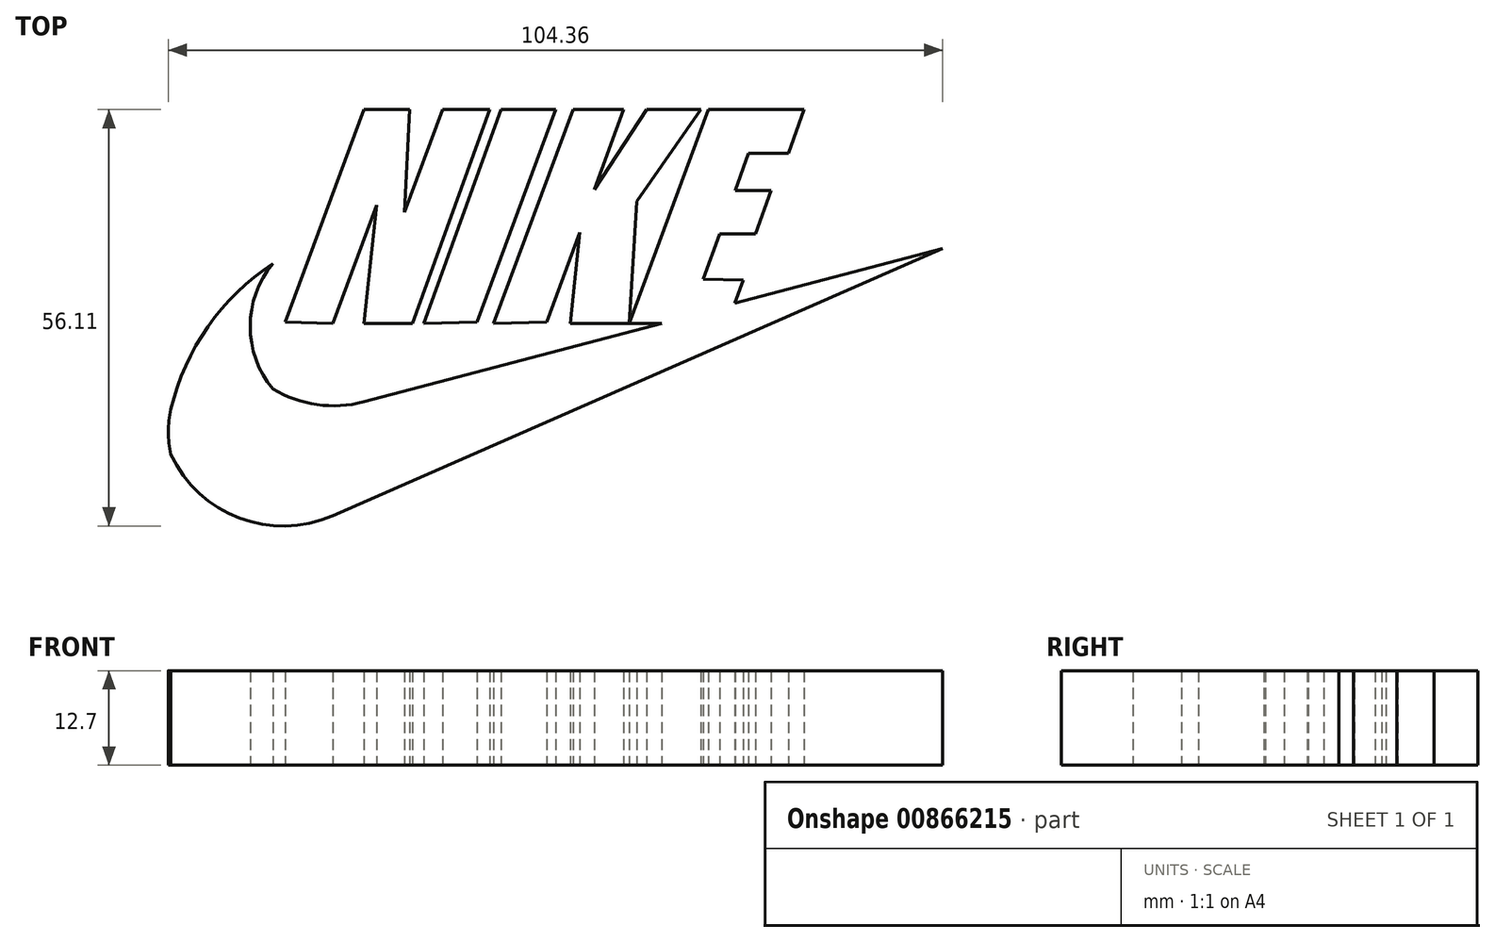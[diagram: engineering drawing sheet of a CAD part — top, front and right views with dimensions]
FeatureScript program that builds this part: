
annotation { "Feature Type Name" : "Feature", "Feature Type Description" : "" }
export const myFeature = defineFeature(function(context is Context, id is Id, definition is map)
    precondition{}
    {
        {
            var Q0;
            Q0=qCreatedBy(makeId("Top.planeOp"),FACE);
            var sketch = newSketch(context, id + "F0", { "sketchPlane" : qUnion([Q0])});
            skLineSegment(sketch, "E0", {"start": v(-47.42, 31.24) * mm, "end": v(-36.81, 59.87) * mm});
            skLineSegment(sketch, "E1", {"start": v(-36.81, 59.87) * mm, "end": v(-30.63, 59.87) * mm});
            skLineSegment(sketch, "E2", {"start": v(-30.63, 59.87) * mm, "end": v(-31.32, 46.03) * mm});
            skLineSegment(sketch, "E3", {"start": v(-31.32, 46.03) * mm, "end": v(-26.16, 59.87) * mm});
            skLineSegment(sketch, "E4", {"start": v(-26.16, 59.87) * mm, "end": v(-19.85, 59.87) * mm});
            skLineSegment(sketch, "E5", {"start": v(-19.85, 59.87) * mm, "end": v(-30.25, 31.03) * mm});
            skLineSegment(sketch, "E6", {"start": v(-30.25, 31.03) * mm, "end": v(-36.81, 31.03) * mm});
            skLineSegment(sketch, "E7", {"start": v(-36.81, 31.03) * mm, "end": v(-35.1, 46.96) * mm});
            skLineSegment(sketch, "E8", {"start": v(-35.1, 46.96) * mm, "end": v(-40.99, 31.03) * mm});
            skLineSegment(sketch, "E9", {"start": v(-40.99, 31.03) * mm, "end": v(-47.42, 31.24) * mm});
            skLineSegment(sketch, "E10", {"start": v(-28.7, 31.03) * mm, "end": v(-18.3, 59.87) * mm});
            skLineSegment(sketch, "E11", {"start": v(-18.3, 59.87) * mm, "end": v(-10.92, 59.87) * mm});
            skLineSegment(sketch, "E12", {"start": v(-10.92, 59.87) * mm, "end": v(-21.53, 31.24) * mm});
            skLineSegment(sketch, "E13", {"start": v(-21.53, 31.24) * mm, "end": v(-28.7, 31.03) * mm});
            skLineSegment(sketch, "E14", {"start": v(-19.3, 31.03) * mm, "end": v(-8.61, 59.87) * mm});
            skLineSegment(sketch, "E15", {"start": v(-8.61, 59.87) * mm, "end": v(-1.83, 59.87) * mm});
            skLineSegment(sketch, "E16", {"start": v(-1.83, 59.87) * mm, "end": v(-5.71, 49.1) * mm});
            skLineSegment(sketch, "E17", {"start": v(-5.71, 49.1) * mm, "end": v(1.3, 59.87) * mm});
            skLineSegment(sketch, "E18", {"start": v(1.3, 59.87) * mm, "end": v(8.6, 59.87) * mm});
            skLineSegment(sketch, "E19", {"start": v(8.6, 59.87) * mm, "end": v(0, 47.53) * mm});
            skLineSegment(sketch, "E20", {"start": v(0, 47.53) * mm, "end": v(-1.04, 31.03) * mm});
            skLineSegment(sketch, "E21", {"start": v(-1.04, 31.03) * mm, "end": v(-9, 31.03) * mm});
            skLineSegment(sketch, "E22", {"start": v(-9, 31.03) * mm, "end": v(-7.69, 43.28) * mm});
            skLineSegment(sketch, "E23", {"start": v(-7.69, 43.28) * mm, "end": v(-12.14, 31.24) * mm});
            skLineSegment(sketch, "E24", {"start": v(-12.14, 31.24) * mm, "end": v(-19.3, 31.03) * mm});
            skLineSegment(sketch, "E25", {"start": v(-1.04, 31.03) * mm, "end": v(9.64, 59.87) * mm});
            skLineSegment(sketch, "E26", {"start": v(9.64, 59.87) * mm, "end": v(22.52, 59.87) * mm});
            skLineSegment(sketch, "E27", {"start": v(22.52, 59.87) * mm, "end": v(20.4, 54) * mm});
            skLineSegment(sketch, "E28", {"start": v(20.4, 54) * mm, "end": v(15.04, 54) * mm});
            skLineSegment(sketch, "E29", {"start": v(15.04, 54) * mm, "end": v(13.23, 48.96) * mm});
            skLineSegment(sketch, "E30", {"start": v(13.23, 48.96) * mm, "end": v(18.06, 48.96) * mm});
            skLineSegment(sketch, "E31", {"start": v(18.06, 48.96) * mm, "end": v(15.96, 43.13) * mm});
            skLineSegment(sketch, "E32", {"start": v(15.96, 43.13) * mm, "end": v(11.13, 43.13) * mm});
            skLineSegment(sketch, "E33", {"start": v(11.13, 43.13) * mm, "end": v(8.94, 37.05) * mm});
            skLineSegment(sketch, "E34", {"start": v(8.94, 37.05) * mm, "end": v(14.32, 36.87) * mm});
            skLineSegment(sketch, "E35", {"start": v(14.32, 36.87) * mm, "end": v(13.2, 33.78) * mm});
            skLineSegment(sketch, "E36", {"start": v(13.2, 33.78) * mm, "end": v(41.2, 41.13) * mm});
            skLineSegment(sketch, "E37", {"start": v(-1.04, 31.03) * mm, "end": v(3.37, 31.03) * mm});
            skLineSegment(sketch, "E38", {"start": v(3.37, 31.03) * mm, "end": v(-36.81, 20.49) * mm});
            skLineSegment(sketch, "E39", {"start": v(41.2, 41.13) * mm, "end": v(-40.99, 5.16) * mm});
            skArc(sketch, "E40", {"start": v(-49.08, 22.21) * mm, "mid": v(-43.12, 20.12) * mm, "end": v(-36.81, 20.49) * mm});
            skArc(sketch, "E41", {"start": v(-49.08, 39.12) * mm, "mid": v(-52.12, 30.67) * mm, "end": v(-49.08, 22.21) * mm});
            skArc(sketch, "E42", {"start": v(-49.08, 39.12) * mm, "mid": v(-57.8, 30.62) * mm, "end": v(-62.8, 19.5) * mm});
            skArc(sketch, "E43", {"start": v(-62.8, 19.5) * mm, "mid": v(-63.16, 16.46) * mm, "end": v(-62.8, 13.42) * mm});
            skArc(sketch, "E44", {"start": v(-62.8, 13.42) * mm, "mid": v(-53.58, 4.84) * mm, "end": v(-40.99, 5.16) * mm});
            skSolve(sketch);
        }
        {
            var Q0;
            Q0=makeQuery(id+"F0.imprint","IMPRINT",FACE,{"disambiguationData":[TD([[makeQuery(id+"F0.imprint","IMPRINT",EDGE,{"derivedFrom":sQuery(id+"F0.wireOp",EDGE,"E0")}),-1.0]])]});
            var Q1;
            Q1=makeQuery(id+"F0.imprint","IMPRINT",FACE,{"disambiguationData":[TD([[makeQuery(id+"F0.imprint","IMPRINT",EDGE,{"derivedFrom":sQuery(id+"F0.wireOp",EDGE,"E10")}),-1.0]])]});
            var Q2;
            Q2=makeQuery(id+"F0.imprint","IMPRINT",FACE,{"disambiguationData":[TD([[makeQuery(id+"F0.imprint","IMPRINT",EDGE,{"derivedFrom":sQuery(id+"F0.wireOp",EDGE,"E14")}),-1.0]])]});
            var Q3;
            Q3=makeQuery(id+"F0.imprint","IMPRINT",FACE,{"disambiguationData":[TD([[makeQuery(id+"F0.imprint","IMPRINT",EDGE,{"derivedFrom":sQuery(id+"F0.wireOp",EDGE,"E25")}),-1.0]])]});
            extrude(context, id + "F1", {"entities" : qUnion([Q0, Q1, Q2, Q3]), "depth" : 12.7 * mm, "offsetDistance" : 25.4 * mm});
        }
    });
